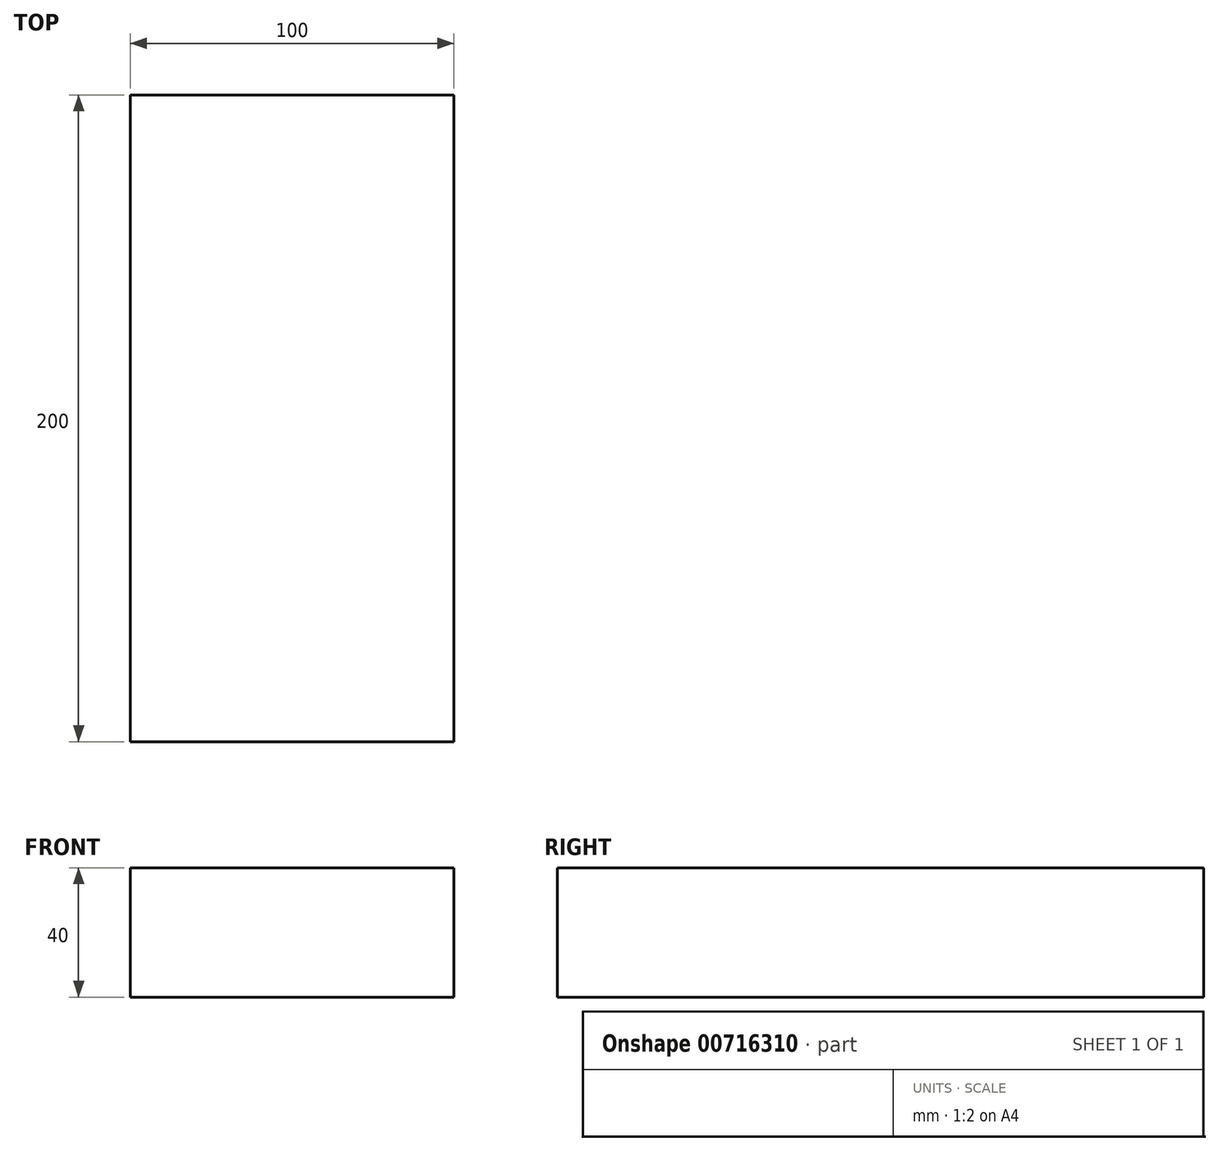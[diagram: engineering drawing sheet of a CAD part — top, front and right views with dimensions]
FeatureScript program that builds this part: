
annotation { "Feature Type Name" : "Feature", "Feature Type Description" : "" }
export const myFeature = defineFeature(function(context is Context, id is Id, definition is map)
    precondition{}
    {
        {
            var Q0;
            Q0=qCreatedBy(makeId("Top.planeOp"),FACE);
            var sketch = newSketch(context, id + "F0", { "sketchPlane" : qUnion([Q0])});
            skLineSegment(sketch, "E0.bottom", {"start": v(50, -100) * mm, "end": v(-50, -100) * mm});
            skLineSegment(sketch, "E0.top", {"start": v(50, 100) * mm, "end": v(-50, 100) * mm});
            skLineSegment(sketch, "E0.left", {"start": v(50, -100) * mm, "end": v(50, 100) * mm});
            skLineSegment(sketch, "E0.right", {"start": v(-50, -100) * mm, "end": v(-50, 100) * mm});
            skPoint(sketch, "E0.middle", {"position": v(0, 0) * mm});
            skSolve(sketch);
        }
        {
            var Q0;
            Q0 = qSketchRegion(id + "F0", true);
            extrude(context, id + "F1", {"entities" : qUnion([Q0]), "depth" : 40 * mm, "offsetDistance" : 25 * mm});
        }
    });
